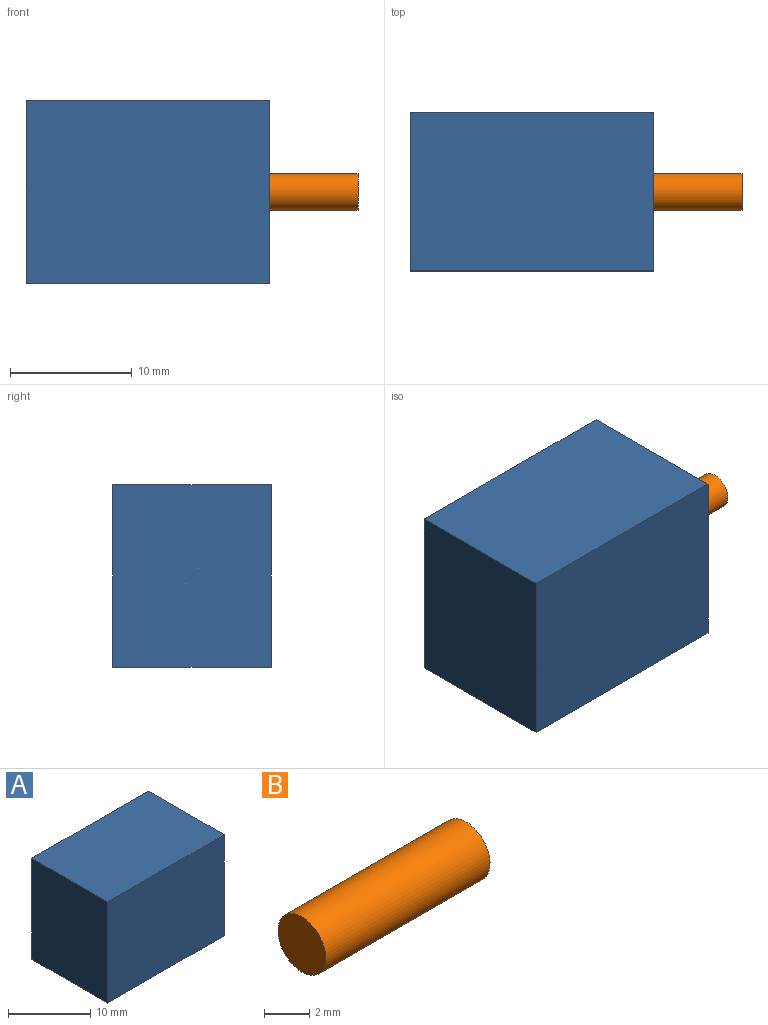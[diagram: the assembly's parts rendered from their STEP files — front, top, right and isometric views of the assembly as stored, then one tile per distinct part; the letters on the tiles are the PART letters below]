
ASSEMBLY  parts=2 mates=1
PART A: 8 faces, bbox 20x13x15 mm
  f0: plane 20x15mm, normal (0,-1,0), area 300mm2, adj f1,f3,f4,f5
  f1: plane 15x13mm, normal (1,0,0), area 187.5mm2, adj f0,f2,f4,f5,f6
  f2: plane 20x15mm, normal (0,1,0), area 300mm2, adj f1,f3,f4,f5
  f3: plane 15x13mm, normal (-1,0,0), area 195mm2, adj f0,f2,f4,f5
  f4: plane 20x13mm, normal (0,0,1), area 260mm2, adj f0,f1,f2,f3
  f5: plane 20x13mm, normal (0,0,-1), area 260mm2, adj f0,f1,f2,f3
  f6: cylinder r=1.55mm len=3.1mm, axis (1,0,0), area 29.2mm2, adj f1,f7
  f7: plane 3.1x3.1mm, normal (1,0,0), area 7.5mm2, adj f6
PART B: 3 faces, bbox 10.3x3x3 mm
  f0: cylinder r=1.5mm len=10.3mm, axis (-1,0,0), area 97.1mm2, adj f1,f2
  f1: plane 3x3mm, normal (1,0,0), area 7.1mm2, adj f0
  f2: plane 3x3mm, normal (-1,0,0), area 7.1mm2, adj f0
PLACE A t=(-7,0,-7.5)mm
PLACE B at identity
MATE revolute A.f6 <-> B.f0  axis (1,0,0) through (0,0,0)mm
